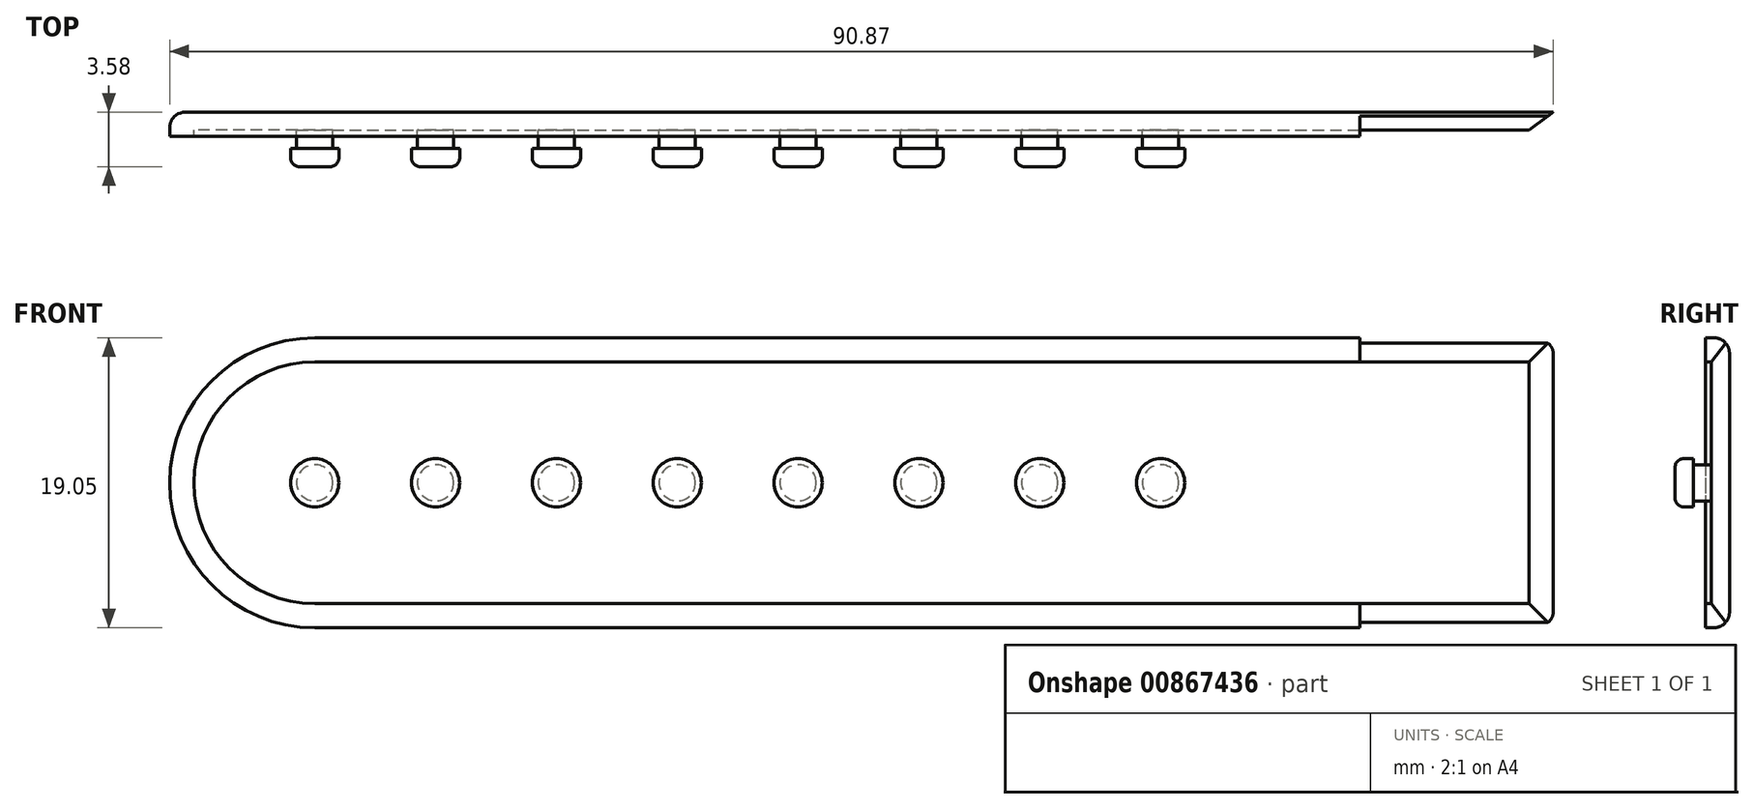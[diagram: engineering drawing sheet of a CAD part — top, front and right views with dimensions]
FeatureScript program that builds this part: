
annotation { "Feature Type Name" : "Feature", "Feature Type Description" : "" }
export const myFeature = defineFeature(function(context is Context, id is Id, definition is map)
    precondition{}
    {
        {
            var Q0;
            Q0=qCreatedBy(makeId("Front.planeOp"),FACE);
            var sketch = newSketch(context, id + "F0", { "sketchPlane" : qUnion([Q0])});
            skLineSegment(sketch, "E0", {"start": v(0, 0) * mm, "end": v(-81.36, 0) * mm});
            skLineSegment(sketch, "E1", {"start": v(0, 19.05) * mm, "end": v(-81.36, 19.05) * mm});
            skArc(sketch, "E2", {"start": v(-81.36, 19.05) * mm, "mid": v(-90.88, 9.52) * mm, "end": v(-81.36, 0) * mm});
            skLineSegment(sketch, "E3", {"start": v(0, 19.05) * mm, "end": v(0, 0) * mm});
            skCircle(sketch, "E4", {"center": v(-73.42, 9.52) * mm, "radius": 1.59 * mm});
            skCircle(sketch, "E5", {"center": v(-65.48, 9.52) * mm, "radius": 1.59 * mm});
            skCircle(sketch, "E6", {"center": v(-57.55, 9.52) * mm, "radius": 1.59 * mm});
            skCircle(sketch, "E7", {"center": v(-49.6, 9.52) * mm, "radius": 1.59 * mm});
            skCircle(sketch, "E8", {"center": v(-41.67, 9.52) * mm, "radius": 1.59 * mm});
            skCircle(sketch, "E9", {"center": v(-33.73, 9.52) * mm, "radius": 1.59 * mm});
            skCircle(sketch, "E10", {"center": v(-81.36, 9.52) * mm, "radius": 1.59 * mm});
            skCircle(sketch, "E11", {"center": v(-25.8, 9.52) * mm, "radius": 1.59 * mm});
            skArc(sketch, "E12", {"start": v(-81.36, 17.46) * mm, "mid": v(-89.3, 9.52) * mm, "end": v(-81.36, 1.59) * mm});
            skCircle(sketch, "E13", {"center": v(-81.36, 9.52) * mm, "radius": 1.2 * mm});
            skCircle(sketch, "E14", {"center": v(-73.42, 9.52) * mm, "radius": 1.2 * mm});
            skCircle(sketch, "E15", {"center": v(-65.48, 9.52) * mm, "radius": 1.2 * mm});
            skCircle(sketch, "E16", {"center": v(-57.55, 9.52) * mm, "radius": 1.2 * mm});
            skCircle(sketch, "E17", {"center": v(-49.6, 9.52) * mm, "radius": 1.2 * mm});
            skCircle(sketch, "E18", {"center": v(-41.67, 9.52) * mm, "radius": 1.2 * mm});
            skCircle(sketch, "E19", {"center": v(-33.73, 9.52) * mm, "radius": 1.2 * mm});
            skCircle(sketch, "E20", {"center": v(-25.8, 9.52) * mm, "radius": 1.2 * mm});
            skLineSegment(sketch, "E21", {"start": v(-81.36, 17.46) * mm, "end": v(-12.7, 17.46) * mm});
            skLineSegment(sketch, "E22", {"start": v(-81.36, 1.59) * mm, "end": v(-12.7, 1.59) * mm});
            skLineSegment(sketch, "E23", {"start": v(-12.7, 17.46) * mm, "end": v(-12.7, 19.05) * mm});
            skLineSegment(sketch, "E24", {"start": v(-12.7, 1.59) * mm, "end": v(-12.7, 0) * mm});
            skLineSegment(sketch, "E25", {"start": v(-12.7, 17.46) * mm, "end": v(-1.59, 17.46) * mm});
            skLineSegment(sketch, "E26", {"start": v(-12.7, 1.59) * mm, "end": v(-1.59, 1.59) * mm});
            skLineSegment(sketch, "E27", {"start": v(-1.59, 17.46) * mm, "end": v(-1.59, 1.59) * mm});
            skSolve(sketch);
        }
        {
            var Q0;
            {var subQ0=sQuery(id+"F0.wireOp",EDGE,"E2");Q0=makeQuery(id+"F0.imprint","IMPRINT",FACE,{"disambiguationData":[TD([[makeQuery(id+"F0.imprint","IMPRINT",EDGE,{"derivedFrom":subQ0}),1.0]])]});}
            extrude(context, id + "F1", {"entities" : qUnion([Q0]), "depth" : 1.59 * mm, "offsetDistance" : 25.4 * mm});
        }
        {
            var Q0;
            Q0=makeQuery(id+"F0.imprint","IMPRINT",FACE,{"disambiguationData":[TD([[makeQuery(id+"F0.imprint","IMPRINT",EDGE,{"derivedFrom":sQuery(id+"F0.wireOp",EDGE,"E12")}),1.0]])]});
            var Q1;
            Q1=makeQuery(id+"F0.imprint","IMPRINT",FACE,{"disambiguationData":[TD([[makeQuery(id+"F0.imprint","IMPRINT",EDGE,{"derivedFrom":sQuery(id+"F0.wireOp",EDGE,"E10")}),1.0]])]});
            var Q2;
            Q2=makeQuery(id+"F0.imprint","IMPRINT",FACE,{"disambiguationData":[TD([[makeQuery(id+"F0.imprint","IMPRINT",EDGE,{"derivedFrom":sQuery(id+"F0.wireOp",EDGE,"E4")}),1.0]])]});
            var Q3;
            Q3=makeQuery(id+"F0.imprint","IMPRINT",FACE,{"disambiguationData":[TD([[makeQuery(id+"F0.imprint","IMPRINT",EDGE,{"derivedFrom":sQuery(id+"F0.wireOp",EDGE,"E5")}),1.0]])]});
            var Q4;
            Q4=makeQuery(id+"F0.imprint","IMPRINT",FACE,{"disambiguationData":[TD([[makeQuery(id+"F0.imprint","IMPRINT",EDGE,{"derivedFrom":sQuery(id+"F0.wireOp",EDGE,"E6")}),1.0]])]});
            var Q5;
            Q5=makeQuery(id+"F0.imprint","IMPRINT",FACE,{"disambiguationData":[TD([[makeQuery(id+"F0.imprint","IMPRINT",EDGE,{"derivedFrom":sQuery(id+"F0.wireOp",EDGE,"E7")}),1.0]])]});
            var Q6;
            Q6=makeQuery(id+"F0.imprint","IMPRINT",FACE,{"disambiguationData":[TD([[makeQuery(id+"F0.imprint","IMPRINT",EDGE,{"derivedFrom":sQuery(id+"F0.wireOp",EDGE,"E8")}),1.0]])]});
            var Q7;
            Q7=makeQuery(id+"F0.imprint","IMPRINT",FACE,{"disambiguationData":[TD([[makeQuery(id+"F0.imprint","IMPRINT",EDGE,{"derivedFrom":sQuery(id+"F0.wireOp",EDGE,"E9")}),1.0]])]});
            var Q8;
            Q8=makeQuery(id+"F0.imprint","IMPRINT",FACE,{"disambiguationData":[TD([[makeQuery(id+"F0.imprint","IMPRINT",EDGE,{"derivedFrom":sQuery(id+"F0.wireOp",EDGE,"E11")}),1.0]])]});
            extrude(context, id + "F2", {"entities" : qUnion([Q0, Q1, Q2, Q3, Q4, Q5, Q6, Q7, Q8]), "operationType" : NewBodyOperationType.ADD, "depth" : 1.19 * mm, "offsetDistance" : 25.4 * mm});
        }
        {
            var Q0;
            {var subQ1=sQuery(id+"F0.wireOp",EDGE,"E3");Q0=makeQuery(id+"F0.imprint","IMPRINT",FACE,{"disambiguationData":[TD([[makeQuery(id+"F0.imprint","IMPRINT",EDGE,{"derivedFrom":subQ1}),-1.0]])]});}
            extrude(context, id + "F3", {"entities" : qUnion([Q0]), "operationType" : NewBodyOperationType.ADD, "depth" : 1.19 * mm, "offsetDistance" : 25.4 * mm});
        }
        {
            var Q0;
            Q0=makeQuery(id+"F3.opExtrude","CAP_EDGE",EDGE,{"disambiguationData":[OSD([sQuery(id+"F0.wireOp",EDGE,"E1")])],"isStart":false});
            var Q1;
            Q1=makeQuery(id+"F3.opExtrude","CAP_EDGE",EDGE,{"disambiguationData":[OSD([sQuery(id+"F0.wireOp",EDGE,"E3")])],"isStart":false});
            var Q2;
            Q2=makeQuery(id+"F3.opExtrude","CAP_EDGE",EDGE,{"disambiguationData":[OSD([sQuery(id+"F0.wireOp",EDGE,"E0")])],"isStart":false});
            chamfer(context, id + "F4", {"entities" : qUnion([Q0, Q1, Q2]), "chamferType" : ChamferType.OFFSET_ANGLE, "width" : 1.59 * mm, "oppositeDirection" : false, "angle" : 37 * degree, "tangentPropagation" : true});
        }
        {
            var Q0;
            Q0=makeQuery(id+"F0.imprint","IMPRINT",FACE,{"disambiguationData":[TD([[makeQuery(id+"F0.imprint","IMPRINT",EDGE,{"derivedFrom":sQuery(id+"F0.wireOp",EDGE,"E13")}),1.0]])]});
            var Q1;
            Q1=makeQuery(id+"F0.imprint","IMPRINT",FACE,{"disambiguationData":[TD([[makeQuery(id+"F0.imprint","IMPRINT",EDGE,{"derivedFrom":sQuery(id+"F0.wireOp",EDGE,"E14")}),1.0]])]});
            var Q2;
            Q2=makeQuery(id+"F0.imprint","IMPRINT",FACE,{"disambiguationData":[TD([[makeQuery(id+"F0.imprint","IMPRINT",EDGE,{"derivedFrom":sQuery(id+"F0.wireOp",EDGE,"E15")}),1.0]])]});
            var Q3;
            Q3=makeQuery(id+"F0.imprint","IMPRINT",FACE,{"disambiguationData":[TD([[makeQuery(id+"F0.imprint","IMPRINT",EDGE,{"derivedFrom":sQuery(id+"F0.wireOp",EDGE,"E16")}),1.0]])]});
            var Q4;
            Q4=makeQuery(id+"F0.imprint","IMPRINT",FACE,{"disambiguationData":[TD([[makeQuery(id+"F0.imprint","IMPRINT",EDGE,{"derivedFrom":sQuery(id+"F0.wireOp",EDGE,"E17")}),1.0]])]});
            var Q5;
            Q5=makeQuery(id+"F0.imprint","IMPRINT",FACE,{"disambiguationData":[TD([[makeQuery(id+"F0.imprint","IMPRINT",EDGE,{"derivedFrom":sQuery(id+"F0.wireOp",EDGE,"E18")}),1.0]])]});
            var Q6;
            Q6=makeQuery(id+"F0.imprint","IMPRINT",FACE,{"disambiguationData":[TD([[makeQuery(id+"F0.imprint","IMPRINT",EDGE,{"derivedFrom":sQuery(id+"F0.wireOp",EDGE,"E19")}),1.0]])]});
            var Q7;
            Q7=makeQuery(id+"F0.imprint","IMPRINT",FACE,{"disambiguationData":[TD([[makeQuery(id+"F0.imprint","IMPRINT",EDGE,{"derivedFrom":sQuery(id+"F0.wireOp",EDGE,"E20")}),1.0]])]});
            extrude(context, id + "F5", {"entities" : qUnion([Q0, Q1, Q2, Q3, Q4, Q5, Q6, Q7]), "operationType" : NewBodyOperationType.ADD, "depth" : 3.58 * mm, "offsetDistance" : 25.4 * mm});
        }
        {
            var Q0;
            Q0=makeQuery(id+"F0.imprint","IMPRINT",FACE,{"disambiguationData":[TD([[makeQuery(id+"F0.imprint","IMPRINT",EDGE,{"derivedFrom":sQuery(id+"F0.wireOp",EDGE,"E10")}),1.0]])]});
            var Q1;
            Q1=makeQuery(id+"F0.imprint","IMPRINT",FACE,{"disambiguationData":[TD([[makeQuery(id+"F0.imprint","IMPRINT",EDGE,{"derivedFrom":sQuery(id+"F0.wireOp",EDGE,"E4")}),1.0]])]});
            var Q2;
            Q2=makeQuery(id+"F0.imprint","IMPRINT",FACE,{"disambiguationData":[TD([[makeQuery(id+"F0.imprint","IMPRINT",EDGE,{"derivedFrom":sQuery(id+"F0.wireOp",EDGE,"E5")}),1.0]])]});
            var Q3;
            Q3=makeQuery(id+"F0.imprint","IMPRINT",FACE,{"disambiguationData":[TD([[makeQuery(id+"F0.imprint","IMPRINT",EDGE,{"derivedFrom":sQuery(id+"F0.wireOp",EDGE,"E6")}),1.0]])]});
            var Q4;
            Q4=makeQuery(id+"F0.imprint","IMPRINT",FACE,{"disambiguationData":[TD([[makeQuery(id+"F0.imprint","IMPRINT",EDGE,{"derivedFrom":sQuery(id+"F0.wireOp",EDGE,"E7")}),1.0]])]});
            var Q5;
            Q5=makeQuery(id+"F0.imprint","IMPRINT",FACE,{"disambiguationData":[TD([[makeQuery(id+"F0.imprint","IMPRINT",EDGE,{"derivedFrom":sQuery(id+"F0.wireOp",EDGE,"E8")}),1.0]])]});
            var Q6;
            Q6=makeQuery(id+"F0.imprint","IMPRINT",FACE,{"disambiguationData":[TD([[makeQuery(id+"F0.imprint","IMPRINT",EDGE,{"derivedFrom":sQuery(id+"F0.wireOp",EDGE,"E9")}),1.0]])]});
            var Q7;
            Q7=makeQuery(id+"F0.imprint","IMPRINT",FACE,{"disambiguationData":[TD([[makeQuery(id+"F0.imprint","IMPRINT",EDGE,{"derivedFrom":sQuery(id+"F0.wireOp",EDGE,"E11")}),1.0]])]});
            var Q8;
            Q8=makeQuery(id+"F5.opExtrude","CAP_FACE",FACE,{"disambiguationData":[OSD([sQuery(id+"F0.wireOp",EDGE,"E13")])],"isStart":false});
            extrude(context, id + "F6", {"entities" : qUnion([Q0, Q1, Q2, Q3, Q4, Q5, Q6, Q7]), "operationType" : NewBodyOperationType.ADD, "depth" : 3.58 * mm, "offsetDistance" : 0.76 * mm, "hasSecondDirection" : true, "secondDirectionBound" : SecondDirectionBoundingType.UP_TO_NEXT, "secondDirectionOppositeDirection" : false, "secondDirectionDepth" : 2.03 * mm, "secondDirectionBoundEntityFace" : qUnion([Q8]), "hasSecondDirectionOffset" : true, "secondDirectionOffsetDistance" : 1.19 * mm, "secondDirectionOffsetOppositeDirection" : true});
        }
        {
            var Q0;
            Q0=makeQuery(id+"F6.opExtrude","CAP_EDGE",EDGE,{"disambiguationData":[OSD([sQuery(id+"F0.wireOp",EDGE,"E10")])],"isStart":false});
            var Q1;
            Q1=makeQuery(id+"F6.opExtrude","CAP_EDGE",EDGE,{"disambiguationData":[OSD([sQuery(id+"F0.wireOp",EDGE,"E4")])],"isStart":false});
            var Q2;
            Q2=makeQuery(id+"F6.opExtrude","CAP_EDGE",EDGE,{"disambiguationData":[OSD([sQuery(id+"F0.wireOp",EDGE,"E5")])],"isStart":false});
            var Q3;
            Q3=makeQuery(id+"F6.opExtrude","CAP_EDGE",EDGE,{"disambiguationData":[OSD([sQuery(id+"F0.wireOp",EDGE,"E6")])],"isStart":false});
            var Q4;
            Q4=makeQuery(id+"F6.opExtrude","CAP_EDGE",EDGE,{"disambiguationData":[OSD([sQuery(id+"F0.wireOp",EDGE,"E7")])],"isStart":false});
            var Q5;
            Q5=makeQuery(id+"F6.opExtrude","CAP_EDGE",EDGE,{"disambiguationData":[OSD([sQuery(id+"F0.wireOp",EDGE,"E8")])],"isStart":false});
            var Q6;
            Q6=makeQuery(id+"F6.opExtrude","CAP_EDGE",EDGE,{"disambiguationData":[OSD([sQuery(id+"F0.wireOp",EDGE,"E9")])],"isStart":false});
            var Q7;
            Q7=makeQuery(id+"F6.opExtrude","CAP_EDGE",EDGE,{"disambiguationData":[OSD([sQuery(id+"F0.wireOp",EDGE,"E11")])],"isStart":false});
            fillet(context, id + "F7", {"entities" : qUnion([Q0, Q1, Q2, Q3, Q4, Q5, Q6, Q7]), "radius" : 0.58 * mm, "tangentPropagation" : true, "allowEdgeOverflow" : false});
        }
        {
            var Q0;
            {var subQ0=sQuery(id+"F0.wireOp",EDGE,"E0");Q0=makeQuery(id+"F3.boolean.opBoolean","MERGE",EDGE,{"derivedFrom":[makeQuery(id+"F1.opExtrude","CAP_EDGE",EDGE,{"disambiguationData":[OSD([subQ0])],"isStart":true}),makeQuery(id+"F3.opExtrude","CAP_EDGE",EDGE,{"disambiguationData":[OSD([subQ0])],"isStart":true})]});}
            var Q1;
            Q1=makeQuery(id+"F1.opExtrude","CAP_EDGE",EDGE,{"disambiguationData":[OSD([sQuery(id+"F0.wireOp",EDGE,"E2")])],"isStart":true});
            var Q2;
            {var subQ0=sQuery(id+"F0.wireOp",EDGE,"E1");Q2=makeQuery(id+"F3.boolean.opBoolean","MERGE",EDGE,{"derivedFrom":[makeQuery(id+"F1.opExtrude","CAP_EDGE",EDGE,{"disambiguationData":[OSD([subQ0])],"isStart":true}),makeQuery(id+"F3.opExtrude","CAP_EDGE",EDGE,{"disambiguationData":[OSD([subQ0])],"isStart":true})]});}
            fillet(context, id + "F8", {"entities" : qUnion([Q0, Q1, Q2]), "radius" : 1.02 * mm, "tangentPropagation" : true, "allowEdgeOverflow" : false});
        }
    });
